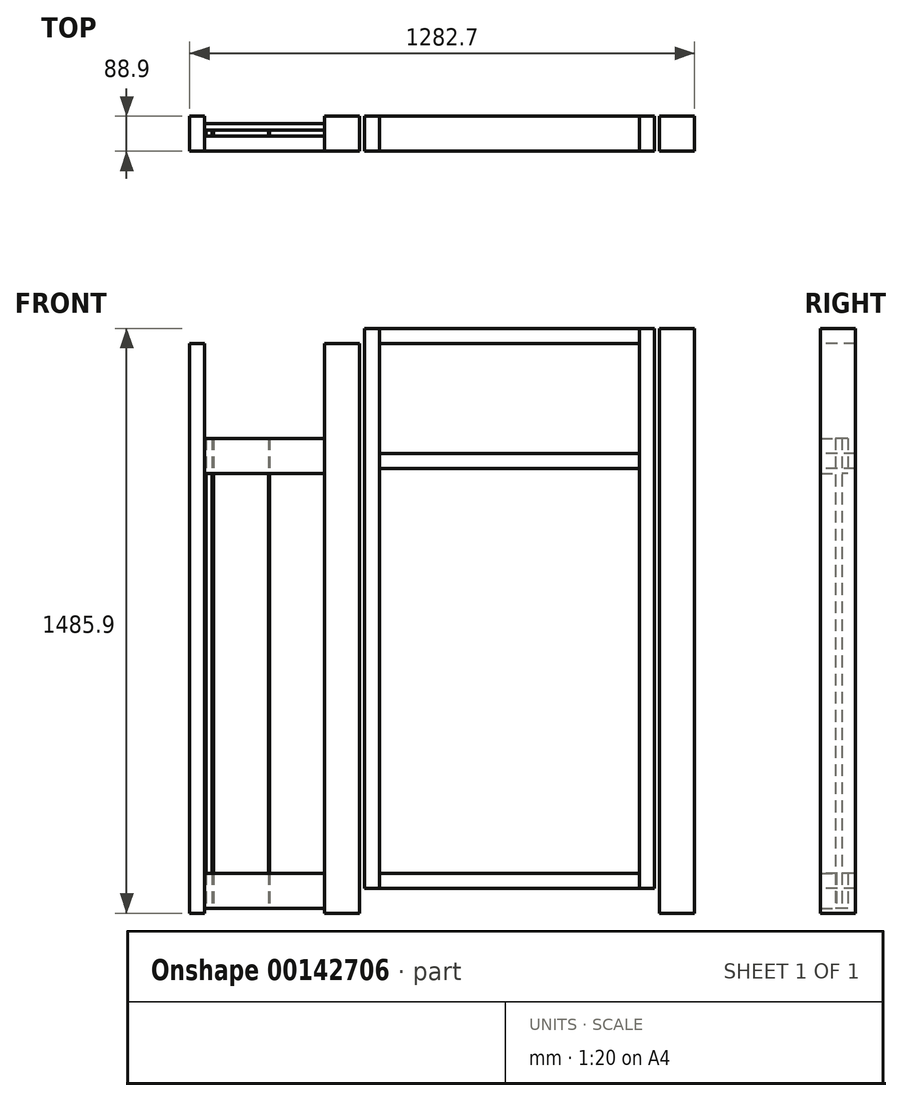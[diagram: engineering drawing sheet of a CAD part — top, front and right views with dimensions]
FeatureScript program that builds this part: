
annotation { "Feature Type Name" : "Feature", "Feature Type Description" : "" }
export const myFeature = defineFeature(function(context is Context, id is Id, definition is map)
    precondition{}
    {
        {
            var Q0;
            Q0=qCreatedBy(makeId("Top.planeOp"),FACE);
            var sketch = newSketch(context, id + "F0", { "sketchPlane" : qUnion([Q0])});
            skLineSegment(sketch, "E0", {"start": v(0, 0) * mm, "end": v(1308.1, 0) * mm, "construction": true});
            skLineSegment(sketch, "E1.bottom", {"start": v(1282.7, 0) * mm, "end": v(1193.8, 0) * mm});
            skLineSegment(sketch, "E1.top", {"start": v(1282.7, 88.9) * mm, "end": v(1193.8, 88.9) * mm});
            skLineSegment(sketch, "E1.left", {"start": v(1282.7, 0) * mm, "end": v(1282.7, 88.9) * mm});
            skLineSegment(sketch, "E1.right", {"start": v(1193.8, 0) * mm, "end": v(1193.8, 88.9) * mm});
            skLineSegment(sketch, "E2.bottom", {"start": v(431.8, 0) * mm, "end": v(342.9, 0) * mm});
            skLineSegment(sketch, "E2.top", {"start": v(431.8, 88.9) * mm, "end": v(342.9, 88.9) * mm});
            skLineSegment(sketch, "E2.left", {"start": v(431.8, 0) * mm, "end": v(431.8, 88.9) * mm});
            skLineSegment(sketch, "E2.right", {"start": v(342.9, 0) * mm, "end": v(342.9, 88.9) * mm});
            skLineSegment(sketch, "E3.bottom", {"start": v(38.1, 0) * mm, "end": v(0, 0) * mm});
            skLineSegment(sketch, "E3.top", {"start": v(38.1, 88.9) * mm, "end": v(0, 88.9) * mm});
            skLineSegment(sketch, "E3.left", {"start": v(38.1, 0) * mm, "end": v(38.1, 88.9) * mm});
            skLineSegment(sketch, "E3.right", {"start": v(0, 0) * mm, "end": v(0, 88.9) * mm});
            skSolve(sketch);
        }
        {
            var Q0;
            Q0 = qSketchRegion(id + "F0", true);
            extrude(context, id + "F1", {"entities" : qUnion([Q0]), "depth" : 1485.9 * mm});
        }
        {
            var Q0;
            Q0=makeQuery(id+"F1.opExtrude","SWEPT_FACE",FACE,{"disambiguationData":[OSD([sQuery(id+"F0.wireOp",EDGE,"E2.right")])]});
            var sketch = newSketch(context, id + "F2", { "sketchPlane" : qUnion([Q0])});
            skLineSegment(sketch, "E4.bottom", {"start": v(0, 1117.6) * mm, "end": v(-38.1, 1117.6) * mm});
            skLineSegment(sketch, "E4.top", {"start": v(0, 1206.5) * mm, "end": v(-38.1, 1206.5) * mm});
            skLineSegment(sketch, "E4.left", {"start": v(0, 1206.5) * mm, "end": v(0, 1117.6) * mm});
            skLineSegment(sketch, "E4.right", {"start": v(-38.1, 1206.5) * mm, "end": v(-38.1, 1117.6) * mm});
            skLineSegment(sketch, "E5.bottom", {"start": v(0, 101.6) * mm, "end": v(-40.45, 101.6) * mm});
            skLineSegment(sketch, "E5.top", {"start": v(0, 12.7) * mm, "end": v(-40.45, 12.7) * mm});
            skLineSegment(sketch, "E5.left", {"start": v(0, 101.6) * mm, "end": v(0, 12.7) * mm});
            skLineSegment(sketch, "E5.right", {"start": v(-40.45, 101.6) * mm, "end": v(-40.45, 12.7) * mm});
            skSolve(sketch);
        }
        {
            var Q0;
            Q0 = qSketchRegion(id + "F2", true);
            extrude(context, id + "F3", {"entities" : qUnion([Q0]), "endBound" : BoundingType.UP_TO_NEXT, "depth" : 25.4 * mm});
        }
        {
            var Q0;
            Q0=makeQuery(id+"F3.opExtrude","SWEPT_FACE",FACE,{"disambiguationData":[OSD([sQuery(id+"F2.wireOp",EDGE,"E4.right")])]});
            var sketch = newSketch(context, id + "F4", { "sketchPlane" : qUnion([Q0])});
            skLineSegment(sketch, "E6.bottom", {"start": v(-342.9, 1206.5) * mm, "end": v(-203.2, 1206.5) * mm});
            skLineSegment(sketch, "E6.top", {"start": v(-342.9, 12.7) * mm, "end": v(-203.2, 12.7) * mm});
            skLineSegment(sketch, "E6.left", {"start": v(-342.9, 1206.5) * mm, "end": v(-342.9, 12.7) * mm});
            skLineSegment(sketch, "E6.right", {"start": v(-203.2, 1206.5) * mm, "end": v(-203.2, 12.7) * mm});
            skLineSegment(sketch, "E7.1.0.0", {"start": v(-60.33, 1206.5) * mm, "end": v(-60.33, 12.7) * mm});
            skLineSegment(sketch, "E7.1.0.1", {"start": v(-200.03, 1206.5) * mm, "end": v(-60.33, 1206.5) * mm});
            skLineSegment(sketch, "E7.1.0.2", {"start": v(-200.03, 1206.5) * mm, "end": v(-200.03, 12.7) * mm});
            skLineSegment(sketch, "E7.1.0.3", {"start": v(-200.02, 12.7) * mm, "end": v(-60.32, 12.7) * mm});
            skLineSegment(sketch, "E7.2.0.1", {"start": v(-57.15, 1206.5) * mm, "end": v(-41.27, 1206.5) * mm});
            skLineSegment(sketch, "E7.2.0.2", {"start": v(-57.15, 1206.5) * mm, "end": v(-57.15, 12.7) * mm});
            skLineSegment(sketch, "E7.2.0.3", {"start": v(-57.15, 12.7) * mm, "end": v(-41.27, 12.7) * mm});
            skLineSegment(sketch, "E7.direction1", {"start": v(-342.9, 12.7) * mm, "end": v(-200.03, 12.7) * mm, "construction": true});
            skLineSegment(sketch, "E8", {"start": v(-41.27, 1206.5) * mm, "end": v(-41.27, 12.7) * mm});
            skSolve(sketch);
        }
        {
            var Q0;
            Q0 = qSketchRegion(id + "F4", true);
            extrude(context, id + "F5", {"entities" : qUnion([Q0]), "depth" : 15.88 * mm});
        }
        {
            var Q0;
            Q0=makeQuery(id+"F5.opExtrude","CAP_FACE",FACE,{"disambiguationData":[OSD([sQuery(id+"F4.wireOp",EDGE,"E6.bottom"),sQuery(id+"F4.wireOp",EDGE,"E6.top"),sQuery(id+"F4.wireOp",EDGE,"E6.left"),sQuery(id+"F4.wireOp",EDGE,"E6.right")])],"isStart":false});
            var sketch = newSketch(context, id + "F6", { "sketchPlane" : qUnion([Q0])});
            skLineSegment(sketch, "E9.bottom", {"start": v(-342.9, 1206.5) * mm, "end": v(-38.1, 1206.5) * mm});
            skLineSegment(sketch, "E9.top", {"start": v(-342.9, 1117.6) * mm, "end": v(-38.1, 1117.6) * mm});
            skLineSegment(sketch, "E9.left", {"start": v(-342.9, 1206.5) * mm, "end": v(-342.9, 1117.6) * mm});
            skLineSegment(sketch, "E9.right", {"start": v(-38.1, 1206.5) * mm, "end": v(-38.1, 1117.6) * mm});
            skLineSegment(sketch, "E10.bottom", {"start": v(-342.9, 12.7) * mm, "end": v(-38.1, 12.7) * mm});
            skLineSegment(sketch, "E10.top", {"start": v(-342.9, 101.6) * mm, "end": v(-38.1, 101.6) * mm});
            skLineSegment(sketch, "E10.left", {"start": v(-342.9, 12.7) * mm, "end": v(-342.9, 101.6) * mm});
            skLineSegment(sketch, "E10.right", {"start": v(-38.1, 12.7) * mm, "end": v(-38.1, 101.6) * mm});
            skSolve(sketch);
        }
        {
            var Q0;
            Q0 = qSketchRegion(id + "F6", true);
            extrude(context, id + "F7", {"entities" : qUnion([Q0]), "depth" : 15.88 * mm});
        }
        {
            var Q0;
            Q0=makeQuery(id+"F1.opExtrude","SWEPT_FACE",FACE,{"disambiguationData":[OSD([sQuery(id+"F0.wireOp",EDGE,"E1.bottom")])]});
            var sketch = newSketch(context, id + "F8", { "sketchPlane" : qUnion([Q0])});
            skLineSegment(sketch, "E11.bottom", {"start": v(1181.1, 1485.9) * mm, "end": v(1143, 1485.9) * mm});
            skLineSegment(sketch, "E11.left", {"start": v(1181.1, 1485.9) * mm, "end": v(1181.1, 63.5) * mm});
            skLineSegment(sketch, "E11.right", {"start": v(1143, 1485.9) * mm, "end": v(1143, 63.5) * mm});
            skLineSegment(sketch, "E12.bottom", {"start": v(482.6, 1485.9) * mm, "end": v(444.5, 1485.9) * mm});
            skLineSegment(sketch, "E12.left", {"start": v(482.6, 1485.9) * mm, "end": v(482.6, 63.5) * mm});
            skLineSegment(sketch, "E12.right", {"start": v(444.5, 1485.9) * mm, "end": v(444.5, 63.5) * mm});
            skLineSegment(sketch, "E13", {"start": v(1181.1, 63.5) * mm, "end": v(1143, 63.5) * mm});
            skLineSegment(sketch, "E14.trimOffspring", {"start": v(482.6, 63.5) * mm, "end": v(444.5, 63.5) * mm});
            skSolve(sketch);
        }
        {
            var Q0;
            Q0 = qSketchRegion(id + "F8", true);
            extrude(context, id + "F9", {"entities" : qUnion([Q0]), "oppositeDirection" : true, "depth" : 88.9 * mm});
        }
        {
            var Q0;
            Q0=makeQuery(id+"F9.opExtrude","CAP_FACE",FACE,{"disambiguationData":[OSD([sQuery(id+"F8.wireOp",EDGE,"E11.bottom"),sQuery(id+"F8.wireOp",EDGE,"E11.top"),sQuery(id+"F8.wireOp",EDGE,"E11.left"),sQuery(id+"F8.wireOp",EDGE,"E11.right")])],"isStart":true});
            var sketch = newSketch(context, id + "F10", { "sketchPlane" : qUnion([Q0])});
            skLineSegment(sketch, "E15.bottom", {"start": v(1143, 1485.9) * mm, "end": v(482.6, 1485.9) * mm});
            skLineSegment(sketch, "E15.top", {"start": v(1143, 1447.8) * mm, "end": v(482.6, 1447.8) * mm});
            skLineSegment(sketch, "E15.left", {"start": v(1143, 1485.9) * mm, "end": v(1143, 1447.8) * mm});
            skLineSegment(sketch, "E15.right", {"start": v(482.6, 1485.9) * mm, "end": v(482.6, 1447.8) * mm});
            skLineSegment(sketch, "E16.bottom", {"start": v(1143, 1168.4) * mm, "end": v(482.6, 1168.4) * mm});
            skLineSegment(sketch, "E16.top", {"start": v(1143, 1130.3) * mm, "end": v(482.6, 1130.3) * mm});
            skLineSegment(sketch, "E16.left", {"start": v(1143, 1168.4) * mm, "end": v(1143, 1130.3) * mm});
            skLineSegment(sketch, "E16.right", {"start": v(482.6, 1168.4) * mm, "end": v(482.6, 1130.3) * mm});
            skLineSegment(sketch, "E17.left", {"start": v(1143, 1447.8) * mm, "end": v(1143, 1485.9) * mm});
            skLineSegment(sketch, "E17.right", {"start": v(482.6, 1447.8) * mm, "end": v(482.6, 1485.9) * mm});
            skLineSegment(sketch, "E18.bottom", {"start": v(1143, 63.5) * mm, "end": v(482.6, 63.5) * mm});
            skLineSegment(sketch, "E18.top", {"start": v(1143, 101.6) * mm, "end": v(482.6, 101.6) * mm});
            skLineSegment(sketch, "E18.left", {"start": v(1143, 63.5) * mm, "end": v(1143, 101.6) * mm});
            skLineSegment(sketch, "E18.right", {"start": v(482.6, 63.5) * mm, "end": v(482.6, 101.6) * mm});
            skSolve(sketch);
        }
        {
            var Q0;
            Q0 = qSketchRegion(id + "F10", true);
            extrude(context, id + "F11", {"entities" : qUnion([Q0]), "oppositeDirection" : true, "depth" : 88.9 * mm});
        }
        {
            var Q0;
            Q0=makeQuery(id+"F1.opExtrude","SWEPT_FACE",FACE,{"disambiguationData":[OSD([sQuery(id+"F0.wireOp",EDGE,"E2.bottom")])]});
            var sketch = newSketch(context, id + "F12", { "sketchPlane" : qUnion([Q0])});
            skLineSegment(sketch, "E19.bottom", {"start": v(0, 1485.9) * mm, "end": v(38.1, 1485.9) * mm});
            skLineSegment(sketch, "E19.top", {"start": v(0, 1447.8) * mm, "end": v(38.1, 1447.8) * mm});
            skLineSegment(sketch, "E19.left", {"start": v(0, 1485.9) * mm, "end": v(0, 1447.8) * mm});
            skLineSegment(sketch, "E19.right", {"start": v(431.8, 1485.9) * mm, "end": v(431.8, 1447.8) * mm});
            skLineSegment(sketch, "E20", {"start": v(38.1, 1485.9) * mm, "end": v(38.1, 1447.8) * mm});
            skLineSegment(sketch, "E21", {"start": v(342.9, 1485.9) * mm, "end": v(342.9, 1447.8) * mm});
            skLineSegment(sketch, "E22.trimOffspring", {"start": v(342.9, 1485.9) * mm, "end": v(431.8, 1485.9) * mm});
            skLineSegment(sketch, "E23.trimOffspring", {"start": v(342.9, 1447.8) * mm, "end": v(431.8, 1447.8) * mm});
            skSolve(sketch);
        }
        {
            var Q0;
            Q0 = qSketchRegion(id + "F12", true);
            extrude(context, id + "F13", {"entities" : qUnion([Q0]), "operationType" : NewBodyOperationType.REMOVE, "oppositeDirection" : true, "depth" : 88.9 * mm});
        }
    });
